# Revit family: E-314_RFA
name_source: partatom
category: Aparatos sanitarios
units: mm (PartAtom-declared; Revit-internal decimal feet)

## family parameters
Activar corte en vistas = No
Compartido = Sí
Corte con vacíos al cargar = No
Cota de conector redondo = Usar diámetro
Mantener orientación de anotación = No
Número OmniClass = 23.45.55.17
Punto de cálculo de habitación = Sí
Se basa en plano de trabajo = No
Siempre vertical = Sí
Tipo de pieza = Normal
Título OmniClass = Mixing Faucets

## types (1)
- E-314
    Acabados = Cromo, Ébano, Titanio, Duna
    Acero Inoxidable = Steel - Polished
    Características = Monomando para fregadero, retráctil con dos tipos
de chorro. COMPONENTES INCLUIDOS:
Llave allen 5/64".
Llave de instalación.
Llave de mantenimiento.
Mangueras flexibles.
Cartucho cerámico de 25 mm con vástago
metálico.
Placa de fijación.
Cubre taladros.
    Comentarios de tipo = Monomando para Fregadero, Retráctil con 2 Tipos de Chorro
    Descripción = Llave de cocina
    Electrónico = Sensor infrarojo: Detección de 1 cm a 7 cm
Tensión de alimentación: 3Vcc
Potencia: 0,2 mW, 2 baterías alcalinas "AAA"
    Elevación por defecto = 35"
    Fabricante = HELVEX S.A. de C.V.
    Garantía = El producto HELVEX está garantizado como
libre de defectos en materiales, mano de obra y
procesos de fabricación.
El producto HELVEX está garantizado,en lo que
se refiere a los acabados, por 10 años para los
acabados Cromo y Duravex, y por 2 años en
acabados diferentes al Cromo y Duravex.
Las piezas que sufren desgaste natural en el
producto están garantizadas para uso
residencial por 5 años, y para uso comercial por
3 años.
La vigencia de la garantía inicia a partir de la
fecha de entrega del producto al consumidor
indicada en la Póliza de Garantía.
    Imagen de tipo = <Ninguno>
    Inlet Threads = ½" - 14 NPSM
    Max. Working Pressure = 14.2 psi
    Min. Working Pressure = 85.3 psi
    Modelo = E-314
    Operación = Para abrir y cerrar el flujo de agua, incline la
palanca.
Para ajustar la temperatura del agua, gire en
sentido de las manecillas del reloj para más
caliente y en sentido contrario a las manecillas
del reloj para más frío.
    Total Height = 15"
    Total Length = 11"
    Total Width = 4"

## geometry (parser evidence)
native form markers: Sweep x3
no freeform markers — native parametric forms only
